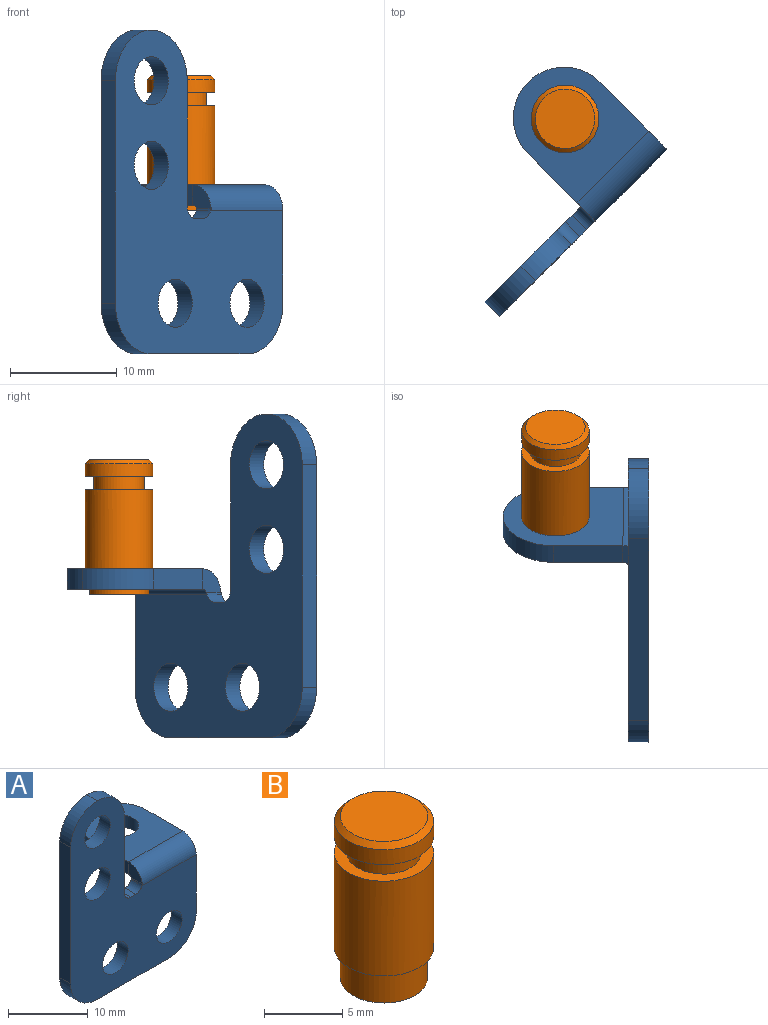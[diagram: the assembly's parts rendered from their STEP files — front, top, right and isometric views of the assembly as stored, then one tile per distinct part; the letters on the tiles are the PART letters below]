
ASSEMBLY  parts=2 mates=1
PART A: 31 faces, bbox 22.2x13.7x30.4 mm
  f0: plane 30.4x22.23mm, normal (0,-1,0), area 374.7mm2, adj f2,f3,f4,f5,f6,f7,f8,f9
  f1: plane 30.4x22.23mm, normal (0,1,0), area 374.7mm2, adj f2,f3,f4,f5,f6,f7,f8,f9
  f2: cylinder r=1.14mm len=1.91mm, axis (0,1,0), area 3.1mm2, adj f0,f1,f7,f17
  f3: plane 20.88x1.91mm, normal (-1,0,0), area 39.8mm2, adj f0,f1,f10,f12
  f4: plane 11.8x1.91mm, normal (1,0,0), area 22.5mm2, adj f0,f1,f8,f9
  f5: plane 8.7x1.91mm, normal (1,0,0), area 16.6mm2, adj f0,f1,f11,f20
  f6: plane 12.7x1.91mm, normal (0,0,-1), area 24.2mm2, adj f0,f1,f11,f12
  f7: plane 1.91x0.89mm, normal (0,0,1), area 1.7mm2, adj f0,f1,f2,f8
  f8: cylinder r=1.14mm len=1.91mm, axis (0,1,0), area 3.4mm2, adj f0,f1,f4,f7
  f9: cylinder r=4.76mm len=4.76mm, axis (0,1,0), area 14.3mm2, adj f0,f1,f4,f10
  f10: cylinder r=4.76mm len=4.76mm, axis (0,1,0), area 14.3mm2, adj f0,f1,f3,f9
  f11: cylinder r=4.76mm len=4.76mm, axis (0,1,0), area 14.3mm2, adj f0,f1,f5,f6
  f12: cylinder r=4.76mm len=4.76mm, axis (0,1,0), area 14.3mm2, adj f0,f1,f3,f6
  f13: cylinder r=2.27mm len=4.53mm, axis (0,1,0), area 27.1mm2, adj f0,f1
  f14: cylinder r=2.27mm len=4.53mm, axis (0,1,0), area 27.1mm2, adj f0,f1
  f15: cylinder r=2.27mm len=4.53mm, axis (0,1,0), area 27.1mm2, adj f0,f1
  f16: cylinder r=2.27mm len=4.53mm, axis (0,1,0), area 27.1mm2, adj f0,f1
  f17: plane 1.91x0.24mm, normal (1,0,0), area 0.5mm2, adj f0,f1,f2,f18
  f18: cylinder r=0mm len=1.91mm, axis (0,-1,0), area 0mm2, adj f0,f1,f17,f19
  f19: plane 1.91x0.01mm, normal (-1,0,0), area 0mm2, adj f0,f1,f18,f21
  f20: plane 2.41x2.41mm, normal (1,0,0), area 4.4mm2, adj f5,f22,f23,f24
  f21: plane 2.41x2.41mm, normal (-1,0,0), area 4.4mm2, adj f19,f22,f23,f25
  f22: cylinder r=2.41mm len=9.53mm, axis (-1,0,0), area 36.1mm2, adj f0,f20,f21,f26
  f23: cylinder r=0.51mm len=9.53mm, axis (-1,0,0), area 7.6mm2, adj f1,f20,f21,f27
  f24: plane 6.49x1.91mm, normal (1,0,0), area 12.4mm2, adj f20,f26,f27,f29
  f25: plane 6.49x1.91mm, normal (-1,0,0), area 12.4mm2, adj f21,f26,f27,f28
  f26: plane 11.25x9.53mm, normal (0,0,1), area 79.6mm2, adj f22,f24,f25,f28,f29,f30
  f27: plane 11.25x9.53mm, normal (0,0,-1), area 79.6mm2, adj f23,f24,f25,f28,f29,f30
  f28: cylinder r=4.76mm len=4.76mm, axis (0,0,-1), area 14.3mm2, adj f25,f26,f27,f29
  f29: cylinder r=4.76mm len=4.76mm, axis (0,0,-1), area 14.3mm2, adj f24,f26,f27,f28
  f30: cylinder r=2.38mm len=4.76mm, axis (0,0,1), area 28.5mm2, adj f26,f27
PART B: 10 faces, bbox 6.4x6.4x12.6 mm
  f0: cylinder r=2.78mm len=5.56mm, axis (0,0,1), area 41.7mm2, adj f1,f3
  f1: plane 5.56x5.56mm, normal (0,0,-1), area 24.3mm2, adj f0
  f2: cylinder r=3.17mm len=7.42mm, axis (0,0,-1), area 148mm2, adj f3,f6
  f3: plane 6.35x6.35mm, normal (0,0,-1), area 7.4mm2, adj f0,f2
  f4: plane 6.35x6.35mm, normal (0,0,-1), area 13.9mm2, adj f5,f9
  f5: cylinder r=2.38mm len=4.76mm, axis (0,0,-1), area 19.4mm2, adj f4,f6
  f6: plane 6.35x6.35mm, normal (0,0,1), area 13.9mm2, adj f2,f5
  f7: plane 5.59x5.59mm, normal (0,0,1), area 24.5mm2, adj f8
  f8: cone r=2.79mm half-angle=45deg, axis (0,0,-1), area 10.1mm2, adj f7,f9
  f9: cylinder r=3.17mm len=6.35mm, axis (0,0,-1), area 23.3mm2, adj f4,f8
PLACE A rot(axis=(0,0,1),44.9deg) t=(15.2,-8.03,5.19)mm
PLACE B rot(axis=(0,0,1),44.9deg) t=(22.72,9.16,21.07)mm
MATE fastened A.f30 <-> B.f0  axis (0,0,1) through (22.72,9.16,21.07)mm
